# Revit family: EF_Veti-4x4-2-Two-Pin-With-1-Switching-1xSingle-Switching-Plug-Point
name_source: partatom
category: Electrical Fixtures
revit_build: Autodesk Revit 2016 (Build: 20150220_1215(x64)
units: mm (PartAtom-declared; Revit-internal decimal feet)

## family parameters
Always vertical = Yes
Cut with Voids When Loaded = No
Maintain Annotation Orientation = No
Part Type = Normal
Room Calculation Point = No
Round Connector Dimension = Use Diameter
Shared = No
Work Plane-Based = No

## types (1)
- 2 Two Pin With 1 Switching  1 x Single Switching Plug Point
    Amperage = 16 A
    Description = 4x4 2 Two Pin With 1 Switching - 1 x Single Switching Plug Point
    Load = 2860 VA
    Made by = Tolani Civil Projects cc
    Manufacturer = VETI
    Switch Voltage = 220 V
    Type Comments = Plug Points
    URL = http://www.major-tech.com
    URL for TCP = http://www.tcpbim.co.za
    Voltage_x = 220 V

## geometry (parser evidence)
native form markers: Sweep x9
no freeform markers — native parametric forms only
